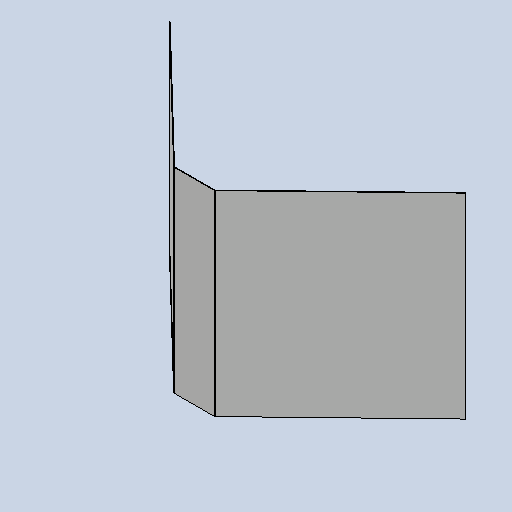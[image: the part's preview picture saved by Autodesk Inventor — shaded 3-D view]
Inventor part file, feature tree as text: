
AUTODESK INVENTOR PART (.ipt)
format: ipt  version: 2025 (Build 290162010, 162A)  size: 241,152 bytes
history: native  units: mm
features: other x4, sheet_metal_op x3, sketch x2, mirror x1
ambient origin geometry x8: Origin, YZ Plane, XZ Plane, XY Plane, X Axis, Y Axis, Z Axis, Center Point
bodies: Solid1 (feature_tree)
feature tree (10):
  sheet_metal_op  "Contour Flange1"
  mirror  "Mirror1"
  other  "Mark1"
  other  "A-Side Definition"
  sketch  "Sketch1"  dims[d7=3.0mm]
  other  "Plate1"
  sheet_metal_op  "Bend1"
  sheet_metal_op  "Corner1"
  sketch  "Sketch2"  dims[d8=3.0mm d9=1.5mm d10=6.0mm d11=3.0mm d12=980.0mm d13=3.0mm d14=3.0mm d15=12.0mm d16=3.0mm d17=3.0mm d25=6.0mm d38=6.0mm d39=3.0mm d40=3.0mm d44=3.0mm d48=742.222353mm d49=23.736478mm d50=100.0mm d51=887.0mm]
  other  "Definition1"
